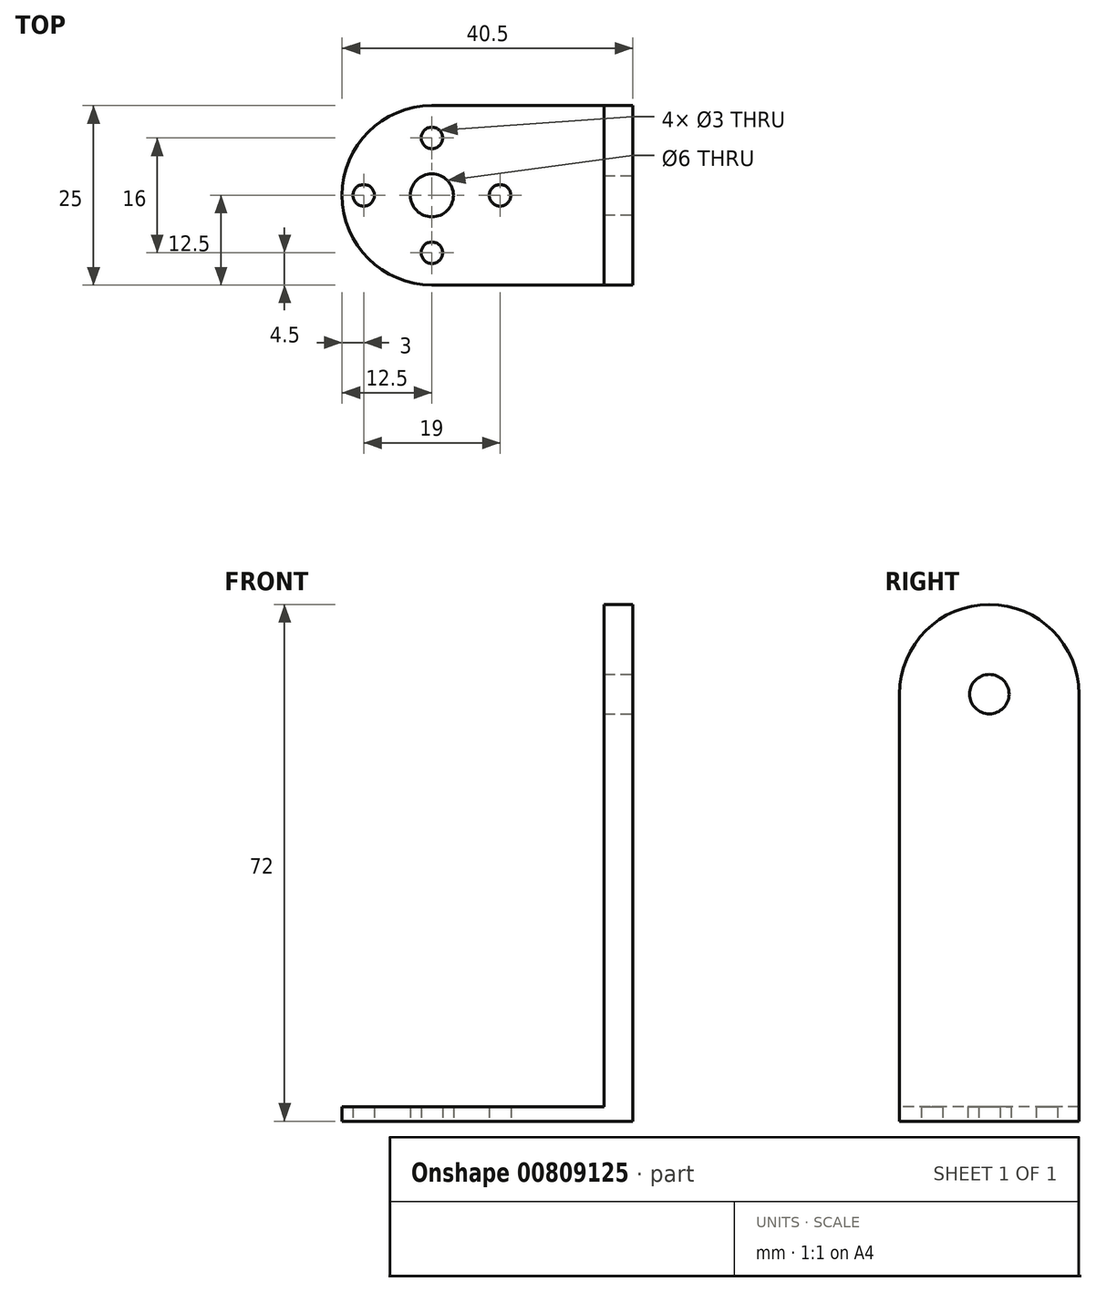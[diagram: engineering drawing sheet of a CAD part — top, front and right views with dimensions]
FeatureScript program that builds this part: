
annotation { "Feature Type Name" : "Feature", "Feature Type Description" : "" }
export const myFeature = defineFeature(function(context is Context, id is Id, definition is map)
    precondition{}
    {
        {
            var Q0;
            Q0=qCreatedBy(makeId("Top.planeOp"),FACE);
            var sketch = newSketch(context, id + "F0", { "sketchPlane" : qUnion([Q0])});
            skPoint(sketch, "E0.middle", {"position": v(0, 0) * mm});
            skCircle(sketch, "E1", {"center": v(0, 0) * mm, "radius": 9.5 * mm});
            skCircle(sketch, "E2", {"center": v(0, 0) * mm, "radius": 8 * mm});
            skCircle(sketch, "E3", {"center": v(0, 0) * mm, "radius": 12.5 * mm});
            skCircle(sketch, "E4", {"center": v(0, 0) * mm, "radius": 3 * mm});
            skLineSegment(sketch, "E5", {"start": v(0, 12.5) * mm, "end": v(28, 12.5) * mm});
            skLineSegment(sketch, "E6", {"start": v(28, 12.5) * mm, "end": v(28, -12.5) * mm});
            skLineSegment(sketch, "E7", {"start": v(28, -12.5) * mm, "end": v(0, -12.5) * mm});
            skCircle(sketch, "E8", {"center": v(0, 8) * mm, "radius": 1.5 * mm});
            skCircle(sketch, "E9", {"center": v(9.5, 0) * mm, "radius": 1.5 * mm});
            skCircle(sketch, "E10", {"center": v(0, -8) * mm, "radius": 1.5 * mm});
            skCircle(sketch, "E11", {"center": v(-9.5, 0) * mm, "radius": 1.5 * mm});
            skSolve(sketch);
        }
        {
            var Q0;
            {var subQ0=sQuery(id+"F0.wireOp",EDGE,"E1");var subQ6=makeQuery(id+"F0.imprint","INTERSECT",VERTEX,{"derivedFrom":[subQ0,sQuery(id+"F0.wireOp",EDGE,"E8")]});Q0=makeQuery(id+"F0.imprint","IMPRINT",FACE,{"disambiguationData":[TD([[makeQuery(id+"F0.imprint","IMPRINT",EDGE,{"disambiguationData":[TD([[subQ6,1.0]])],"derivedFrom":subQ0}),-1.0]])]});}
            var Q1;
            Q1=makeQuery(id+"F0.imprint","IMPRINT",FACE,{"disambiguationData":[TD([[makeQuery(id+"F0.imprint","IMPRINT",EDGE,{"derivedFrom":sQuery(id+"F0.wireOp",EDGE,"E4")}),-1.0]])]});
            var Q2;
            {var subQ0=sQuery(id+"F0.wireOp",EDGE,"E5");Q2=makeQuery(id+"F0.imprint","IMPRINT",FACE,{"disambiguationData":[TD([[makeQuery(id+"F0.imprint","IMPRINT",EDGE,{"derivedFrom":subQ0}),-1.0]])]});}
            var Q3;
            {var subQ0=sQuery(id+"F0.wireOp",EDGE,"E8");var subQ1=sQuery(id+"F0.wireOp",EDGE,"E1");var subQ2=makeQuery(id+"F0.imprint","INTERSECT",VERTEX,{"derivedFrom":[subQ1,subQ0]});Q3=makeQuery(id+"F0.imprint","IMPRINT",FACE,{"disambiguationData":[TD([[makeQuery(id+"F0.imprint","IMPRINT",EDGE,{"disambiguationData":[TD([[subQ2,-1.0]])],"derivedFrom":subQ1}),1.0]])]});}
            var Q4;
            {var subQ0=sQuery(id+"F0.wireOp",EDGE,"E8");var subQ1=sQuery(id+"F0.wireOp",EDGE,"E1");var subQ2=makeQuery(id+"F0.imprint","INTERSECT",VERTEX,{"derivedFrom":[subQ1,subQ0]});Q4=makeQuery(id+"F0.imprint","IMPRINT",FACE,{"disambiguationData":[TD([[makeQuery(id+"F0.imprint","IMPRINT",EDGE,{"disambiguationData":[TD([[subQ2,1.0]])],"derivedFrom":subQ1}),1.0]])]});}
            var Q5;
            {var subQ0=sQuery(id+"F0.wireOp",EDGE,"E10");var subQ1=sQuery(id+"F0.wireOp",EDGE,"E1");var subQ2=makeQuery(id+"F0.imprint","INTERSECT",VERTEX,{"derivedFrom":[subQ1,subQ0]});Q5=makeQuery(id+"F0.imprint","IMPRINT",FACE,{"disambiguationData":[TD([[makeQuery(id+"F0.imprint","IMPRINT",EDGE,{"disambiguationData":[TD([[subQ2,-1.0]])],"derivedFrom":subQ1}),1.0]])]});}
            var Q6;
            {var subQ0=sQuery(id+"F0.wireOp",EDGE,"E11");var subQ1=sQuery(id+"F0.wireOp",EDGE,"E1");var subQ2=makeQuery(id+"F0.imprint","INTERSECT",VERTEX,{"disambiguationData":[OD(1.0)],"derivedFrom":[subQ1,subQ0]});Q6=makeQuery(id+"F0.imprint","IMPRINT",FACE,{"disambiguationData":[TD([[makeQuery(id+"F0.imprint","IMPRINT",EDGE,{"disambiguationData":[TD([[subQ2,-1.0]])],"derivedFrom":subQ1}),1.0]])]});}
            extrude(context, id + "F1", {"entities" : qUnion([Q0, Q1, Q2, Q3, Q4, Q5, Q6]), "depth" : 2 * mm, "offsetDistance" : 25.4 * mm});
        }
        {
            var Q0;
            Q0=makeQuery(id+"F1.opExtrude","CAP_FACE",FACE,{"disambiguationData":[OSD([sQuery(id+"F0.wireOp",EDGE,"JXmqnhbx-AOSX-TyZE-XGMA-spSnwN2CYmG1"),sQuery(id+"F0.wireOp",EDGE,"L4s5CNPj-R1ox-tPac-DCpk-V61URNqcwuZp"),sQuery(id+"F0.wireOp",EDGE,"dKkBehY6-tAzj-RF3e-5FBY-Y6aT0vyPt1sI"),sQuery(id+"F0.wireOp",EDGE,"E3"),sQuery(id+"F0.wireOp",EDGE,"E4"),sQuery(id+"F0.wireOp",EDGE,"0cFATqPL-y9sd-LwLA-wtbT-jdmLwFNByHvY"),sQuery(id+"F0.wireOp",EDGE,"E5"),sQuery(id+"F0.wireOp",EDGE,"E6"),sQuery(id+"F0.wireOp",EDGE,"E7")])],"isStart":false});
            var sketch = newSketch(context, id + "F2", { "sketchPlane" : qUnion([Q0])});
            skLineSegment(sketch, "E12", {"start": v(24, 12.5) * mm, "end": v(24, -12.5) * mm});
            skSolve(sketch);
        }
        {
            var Q0;
            Q0=qSketchRegion(id+"F2",true);
            var Q1;
            {var subQ0=sQuery(id+"F2.wireOp",EDGE,"E12");Q1=makeQuery(id+"F2.imprint","IMPRINT",FACE,{"disambiguationData":[TD([[makeQuery(id+"F2.imprint","IMPRINT",EDGE,{"derivedFrom":subQ0}),1.0]])]});}
            extrude(context, id + "F3", {"entities" : qUnion([Q0, Q1]), "operationType" : NewBodyOperationType.ADD, "depth" : 70 * mm, "offsetDistance" : 25.4 * mm});
        }
        {
            var Q0;
            {var subQ0=sQuery(id+"F0.wireOp",EDGE,"E6");Q0=makeQuery(id+"F3.boolean.opBoolean","MERGE",FACE,{"derivedFrom":[makeQuery(id+"F1.opExtrude","SWEPT_FACE",FACE,{"disambiguationData":[OSD([subQ0])]}),makeQuery(id+"F3.opExtrude","SWEPT_FACE",FACE,{"disambiguationData":[OSD([subQ0])]})]});}
            var sketch = newSketch(context, id + "F4", { "sketchPlane" : qUnion([Q0])});
            skCircle(sketch, "E13", {"center": v(0, 59.5) * mm, "radius": 2.75 * mm});
            skLineSegment(sketch, "E14", {"start": v(0, 59.5) * mm, "end": v(0, 72) * mm, "construction": true});
            skLineSegment(sketch, "E15", {"start": v(0, 59.5) * mm, "end": v(12.5, 59.5) * mm, "construction": true});
            skSolve(sketch);
        }
        {
            var Q0;
            Q0=makeQuery(id+"F4.imprint","IMPRINT",FACE,{"disambiguationData":[TD([[makeQuery(id+"F4.imprint","IMPRINT",EDGE,{"derivedFrom":sQuery(id+"F4.wireOp",EDGE,"E13")}),1.0]])]});
            extrude(context, id + "F5", {"entities" : qUnion([Q0]), "operationType" : NewBodyOperationType.REMOVE, "endBound" : BoundingType.THROUGH_ALL, "oppositeDirection" : true, "depth" : 25.4 * mm, "offsetDistance" : 25.4 * mm});
        }
        {
            var Q0;
            Q0=makeQuery(id+"F3.opExtrude","CAP_EDGE",EDGE,{"disambiguationData":[OSD([sQuery(id+"F2.wireOp",EDGE,"E12")])],"isStart":true});
            var Q1;
            Q1=makeQuery(id+"F3.opExtrude","CAP_EDGE",EDGE,{"disambiguationData":[OSD([sQuery(id+"F0.wireOp",EDGE,"E7")])],"isStart":false});
            var Q2;
            Q2=makeQuery(id+"F3.opExtrude","CAP_EDGE",EDGE,{"disambiguationData":[OSD([sQuery(id+"F0.wireOp",EDGE,"E5")])],"isStart":false});
            fillet(context, id + "F6", {"entities" : qUnion([Q0, Q1, Q2]), "radius" : 12.5 * mm, "tangentPropagation" : true, "allowEdgeOverflow" : false});
        }
    });
